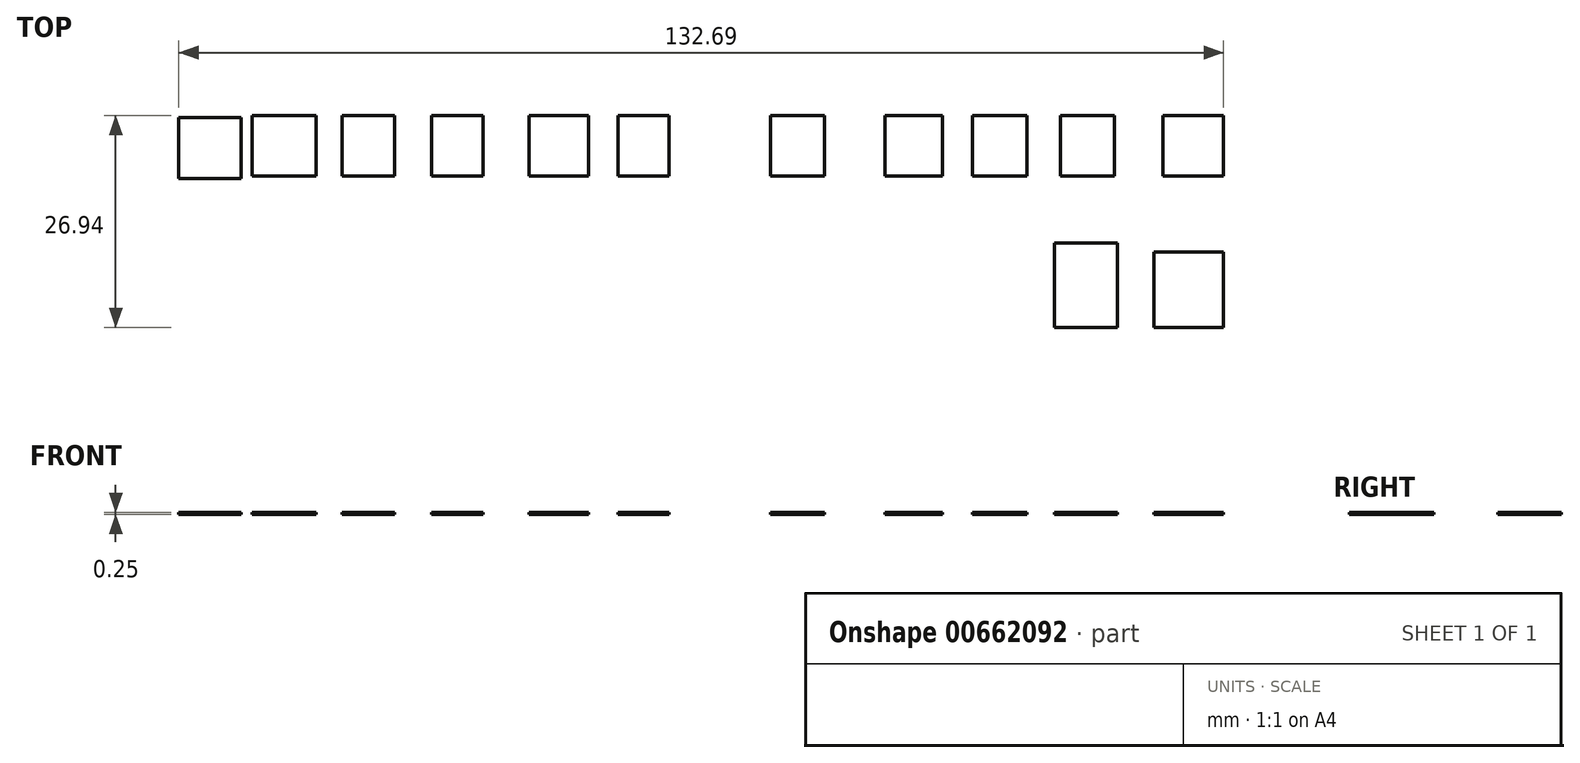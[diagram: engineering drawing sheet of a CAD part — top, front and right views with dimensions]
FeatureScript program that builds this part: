
annotation { "Feature Type Name" : "Feature", "Feature Type Description" : "" }
export const myFeature = defineFeature(function(context is Context, id is Id, definition is map)
    precondition{}
    {
        {
            var Q0;
            Q0=qCreatedBy(makeId("Top.planeOp"),FACE);
            var sketch = newSketch(context, id + "F0", { "sketchPlane" : qUnion([Q0])});
            skLineSegment(sketch, "E0.bottom", {"start": v(-65.37, 61.68) * mm, "end": v(-57.47, 61.68) * mm});
            skLineSegment(sketch, "E0.top", {"start": v(-65.37, 53.94) * mm, "end": v(-57.47, 53.94) * mm});
            skLineSegment(sketch, "E0.left", {"start": v(-65.37, 61.68) * mm, "end": v(-65.37, 53.94) * mm});
            skLineSegment(sketch, "E0.right", {"start": v(-57.47, 61.68) * mm, "end": v(-57.47, 53.94) * mm});
            skSolve(sketch);
        }
        {
            var Q0;
            Q0=makeQuery(id+"F0.imprint","IMPRINT",FACE,{"disambiguationData":[TD([[makeQuery(id+"F0.imprint","IMPRINT",EDGE,{"derivedFrom":sQuery(id+"F0.wireOp",EDGE,"E0.bottom")}),-1.0]])]});
            extrude(context, id + "F1", {"entities" : qUnion([Q0]), "depth" : 0.25 * mm, "offsetDistance" : 25.4 * mm});
        }
        {
            var Q0;
            Q0=qCreatedBy(makeId("Top.planeOp"),FACE);
            var sketch = newSketch(context, id + "F2", { "sketchPlane" : qUnion([Q0])});
            skLineSegment(sketch, "E1.bottom", {"start": v(-56.08, 61.98) * mm, "end": v(-47.95, 61.98) * mm});
            skLineSegment(sketch, "E1.top", {"start": v(-56.08, 54.31) * mm, "end": v(-47.95, 54.31) * mm});
            skLineSegment(sketch, "E1.left", {"start": v(-56.08, 61.98) * mm, "end": v(-56.08, 54.31) * mm});
            skLineSegment(sketch, "E1.right", {"start": v(-47.95, 61.98) * mm, "end": v(-47.95, 54.31) * mm});
            skLineSegment(sketch, "E2.bottom", {"start": v(-44.61, 61.98) * mm, "end": v(-37.97, 61.98) * mm});
            skLineSegment(sketch, "E2.top", {"start": v(-44.61, 54.31) * mm, "end": v(-37.97, 54.31) * mm});
            skLineSegment(sketch, "E2.left", {"start": v(-44.61, 61.98) * mm, "end": v(-44.61, 54.31) * mm});
            skLineSegment(sketch, "E2.right", {"start": v(-37.97, 61.98) * mm, "end": v(-37.97, 54.31) * mm});
            skLineSegment(sketch, "E3.bottom", {"start": v(-33.27, 61.98) * mm, "end": v(-26.7, 61.98) * mm});
            skLineSegment(sketch, "E3.top", {"start": v(-33.27, 54.31) * mm, "end": v(-26.7, 54.31) * mm});
            skLineSegment(sketch, "E3.left", {"start": v(-33.27, 61.98) * mm, "end": v(-33.27, 54.31) * mm});
            skLineSegment(sketch, "E3.right", {"start": v(-26.7, 61.98) * mm, "end": v(-26.7, 54.31) * mm});
            skLineSegment(sketch, "E4.bottom", {"start": v(-20.9, 61.98) * mm, "end": v(-13.31, 61.98) * mm});
            skLineSegment(sketch, "E4.top", {"start": v(-20.9, 54.31) * mm, "end": v(-13.31, 54.31) * mm});
            skLineSegment(sketch, "E4.left", {"start": v(-20.9, 61.98) * mm, "end": v(-20.9, 54.31) * mm});
            skLineSegment(sketch, "E4.right", {"start": v(-13.31, 61.98) * mm, "end": v(-13.31, 54.31) * mm});
            skLineSegment(sketch, "E5.bottom", {"start": v(-9.56, 61.98) * mm, "end": v(-3.08, 61.98) * mm});
            skLineSegment(sketch, "E5.top", {"start": v(-9.56, 54.31) * mm, "end": v(-3.08, 54.31) * mm});
            skLineSegment(sketch, "E5.left", {"start": v(-9.56, 61.98) * mm, "end": v(-9.56, 54.31) * mm});
            skLineSegment(sketch, "E5.right", {"start": v(-3.08, 61.98) * mm, "end": v(-3.08, 54.31) * mm});
            skPoint(sketch, "E6.oppositeSnap0", {"position": v(-6.32, 54.31) * mm});
            skLineSegment(sketch, "E6.bottom", {"start": v(9.77, 61.98) * mm, "end": v(16.68, 61.98) * mm});
            skLineSegment(sketch, "E6.top", {"start": v(9.77, 54.31) * mm, "end": v(16.68, 54.31) * mm});
            skLineSegment(sketch, "E6.left", {"start": v(9.77, 61.98) * mm, "end": v(9.77, 54.31) * mm});
            skLineSegment(sketch, "E6.right", {"start": v(16.68, 61.98) * mm, "end": v(16.68, 54.31) * mm});
            skLineSegment(sketch, "E7.bottom", {"start": v(24.35, 61.98) * mm, "end": v(31.64, 61.98) * mm});
            skLineSegment(sketch, "E7.top", {"start": v(24.35, 54.31) * mm, "end": v(31.64, 54.31) * mm});
            skLineSegment(sketch, "E7.left", {"start": v(24.35, 61.98) * mm, "end": v(24.35, 54.31) * mm});
            skLineSegment(sketch, "E7.right", {"start": v(31.64, 61.98) * mm, "end": v(31.64, 54.31) * mm});
            skLineSegment(sketch, "E8.bottom", {"start": v(35.47, 61.98) * mm, "end": v(42.38, 61.98) * mm});
            skLineSegment(sketch, "E8.top", {"start": v(35.47, 54.31) * mm, "end": v(42.38, 54.31) * mm});
            skLineSegment(sketch, "E8.left", {"start": v(35.47, 61.98) * mm, "end": v(35.47, 54.31) * mm});
            skLineSegment(sketch, "E8.right", {"start": v(42.38, 61.98) * mm, "end": v(42.38, 54.31) * mm});
            skLineSegment(sketch, "E9.bottom", {"start": v(46.6, 61.98) * mm, "end": v(53.5, 61.98) * mm});
            skLineSegment(sketch, "E9.top", {"start": v(46.6, 54.31) * mm, "end": v(53.5, 54.31) * mm});
            skLineSegment(sketch, "E9.left", {"start": v(46.6, 61.98) * mm, "end": v(46.6, 54.31) * mm});
            skLineSegment(sketch, "E9.right", {"start": v(53.5, 61.98) * mm, "end": v(53.5, 54.31) * mm});
            skLineSegment(sketch, "E10.bottom", {"start": v(59.65, 61.98) * mm, "end": v(67.32, 61.98) * mm});
            skLineSegment(sketch, "E10.top", {"start": v(59.65, 54.31) * mm, "end": v(67.32, 54.31) * mm});
            skLineSegment(sketch, "E10.left", {"start": v(59.65, 61.98) * mm, "end": v(59.65, 54.31) * mm});
            skLineSegment(sketch, "E10.right", {"start": v(67.32, 61.98) * mm, "end": v(67.32, 54.31) * mm});
            skLineSegment(sketch, "E11.bottom", {"start": v(67.32, 44.63) * mm, "end": v(58.5, 44.63) * mm});
            skLineSegment(sketch, "E11.top", {"start": v(67.32, 35.04) * mm, "end": v(58.5, 35.04) * mm});
            skLineSegment(sketch, "E11.left", {"start": v(67.32, 44.63) * mm, "end": v(67.32, 35.04) * mm});
            skLineSegment(sketch, "E11.right", {"start": v(58.5, 44.63) * mm, "end": v(58.5, 35.04) * mm});
            skLineSegment(sketch, "E12.bottom", {"start": v(53.9, 45.78) * mm, "end": v(45.83, 45.78) * mm});
            skLineSegment(sketch, "E12.top", {"start": v(53.9, 35.04) * mm, "end": v(45.83, 35.04) * mm});
            skLineSegment(sketch, "E12.left", {"start": v(53.9, 45.78) * mm, "end": v(53.9, 35.04) * mm});
            skLineSegment(sketch, "E12.right", {"start": v(45.83, 45.78) * mm, "end": v(45.83, 35.04) * mm});
            skSolve(sketch);
        }
        {
            var Q0;
            Q0 = qSketchRegion(id + "F2", true);
            extrude(context, id + "F3", {"entities" : qUnion([Q0]), "depth" : 0.25 * mm, "offsetDistance" : 25.4 * mm});
        }
    });
